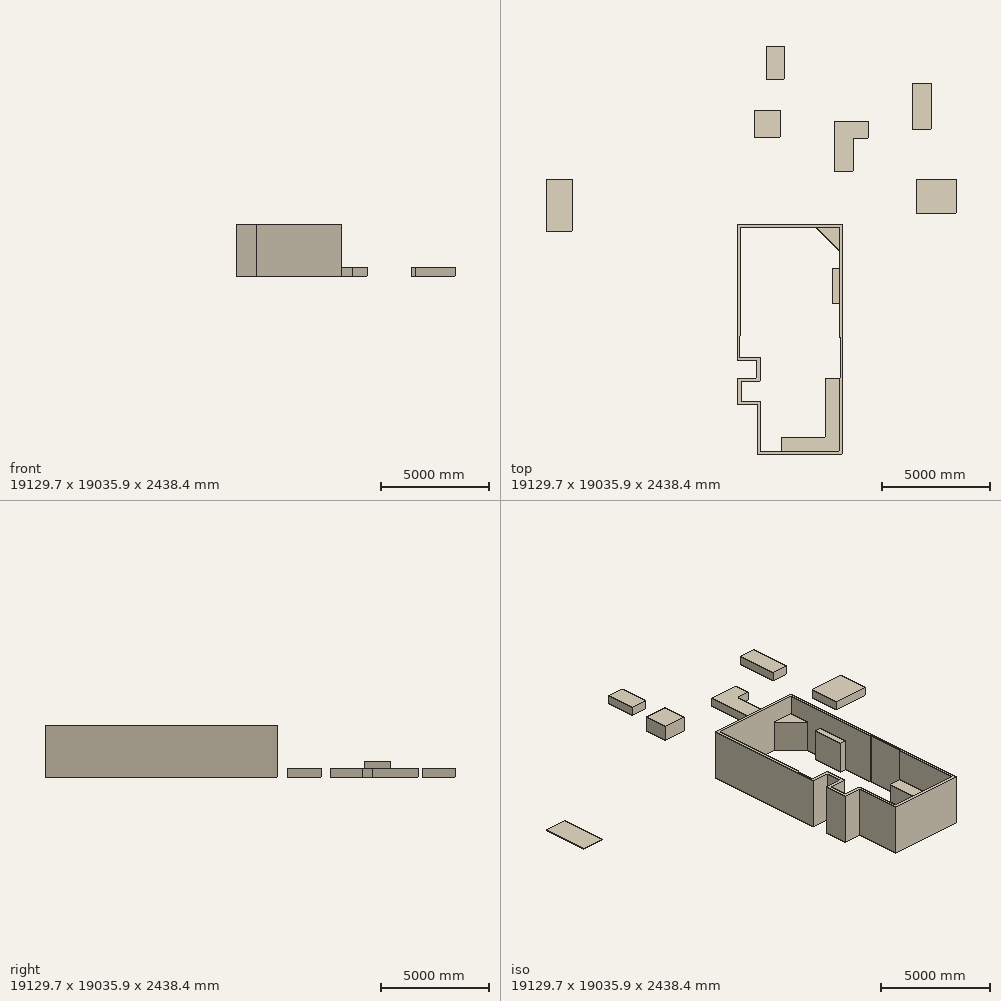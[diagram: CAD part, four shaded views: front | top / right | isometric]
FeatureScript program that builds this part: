
annotation { "Feature Type Name" : "Feature", "Feature Type Description" : "" }
export const myFeature = defineFeature(function(context is Context, id is Id, definition is map)
    precondition{}
    {
        {
            var Q0;
            Q0=qCreatedBy(makeId("Top.planeOp"),FACE);
            var sketch = newSketch(context, id + "F0", { "sketchPlane" : qUnion([Q0])});
            skLineSegment(sketch, "E0", {"start": v(-32.68, 52.66) * mm, "end": v(4583.77, 52.66) * mm});
            skLineSegment(sketch, "E1", {"start": v(4583.77, -10393.09) * mm, "end": v(4583.77, 52.66) * mm});
            skLineSegment(sketch, "E2", {"start": v(-32.68, 52.66) * mm, "end": v(-32.68, -5027.34) * mm});
            skLineSegment(sketch, "E3", {"start": v(-32.68, -5027.34) * mm, "end": v(-32.68, -6017.94) * mm});
            skLineSegment(sketch, "E4", {"start": v(-32.68, -6017.94) * mm, "end": v(894.42, -6017.94) * mm});
            skLineSegment(sketch, "E5", {"start": v(894.42, -6017.94) * mm, "end": v(894.42, -7134.23) * mm});
            skLineSegment(sketch, "E6", {"start": v(894.42, -7134.23) * mm, "end": v(0, -7134.23) * mm});
            skLineSegment(sketch, "E7", {"start": v(0, -7134.23) * mm, "end": v(0, -8060.89) * mm});
            skLineSegment(sketch, "E8", {"start": v(0, -8060.89) * mm, "end": v(929.64, -8060.89) * mm});
            skLineSegment(sketch, "E9", {"start": v(929.64, -8060.89) * mm, "end": v(929.64, -10405.79) * mm});
            skLineSegment(sketch, "E10", {"start": v(929.64, -10393.09) * mm, "end": v(1878.67, -10393.09) * mm});
            skLineSegment(sketch, "E11", {"start": v(1878.67, -10393.09) * mm, "end": v(4583.77, -10393.09) * mm});
            skLineSegment(sketch, "E12.0", {"start": v(1878.67, -10545.49) * mm, "end": v(4736.17, -10545.49) * mm});
            skLineSegment(sketch, "E12.1", {"start": v(-185.08, -6170.34) * mm, "end": v(742.02, -6170.34) * mm});
            skLineSegment(sketch, "E12.2", {"start": v(-185.08, -5040.04) * mm, "end": v(-185.08, -6170.34) * mm});
            skLineSegment(sketch, "E12.3", {"start": v(-185.08, 205.06) * mm, "end": v(-185.08, -5040.04) * mm});
            skLineSegment(sketch, "E12.4", {"start": v(-185.08, 205.06) * mm, "end": v(4736.17, 205.06) * mm});
            skLineSegment(sketch, "E12.5", {"start": v(742.02, -6170.34) * mm, "end": v(742.02, -6981.83) * mm});
            skLineSegment(sketch, "E12.6", {"start": v(4736.17, -10545.49) * mm, "end": v(4736.17, 205.06) * mm});
            skLineSegment(sketch, "E12.7", {"start": v(742.02, -6981.83) * mm, "end": v(-152.4, -6981.83) * mm});
            skLineSegment(sketch, "E12.8", {"start": v(-152.4, -6981.83) * mm, "end": v(-152.4, -8213.29) * mm});
            skLineSegment(sketch, "E12.9", {"start": v(-152.4, -8213.29) * mm, "end": v(777.24, -8213.29) * mm});
            skLineSegment(sketch, "E12.10", {"start": v(777.24, -8213.29) * mm, "end": v(777.24, -10545.49) * mm});
            skLineSegment(sketch, "E12.11", {"start": v(777.24, -10545.49) * mm, "end": v(1878.67, -10545.49) * mm});
            skLineSegment(sketch, "E13.bottom", {"start": v(2045.21, 8490.4) * mm, "end": v(1165.74, 8490.4) * mm});
            skLineSegment(sketch, "E13.top", {"start": v(2045.21, 6960.06) * mm, "end": v(1165.74, 6960.06) * mm});
            skLineSegment(sketch, "E13.left", {"start": v(2045.21, 8490.4) * mm, "end": v(2045.21, 6960.06) * mm});
            skLineSegment(sketch, "E13.right", {"start": v(1165.74, 8490.4) * mm, "end": v(1165.74, 6960.06) * mm});
            skLineSegment(sketch, "E14", {"start": v(4358.78, 4979.33) * mm, "end": v(4358.78, 2667.93) * mm});
            skLineSegment(sketch, "E15", {"start": v(4358.78, 2667.93) * mm, "end": v(5238.26, 2667.93) * mm});
            skLineSegment(sketch, "E16", {"start": v(5238.26, 2667.93) * mm, "end": v(5238.26, 4179.23) * mm});
            skLineSegment(sketch, "E17", {"start": v(5238.26, 4179.23) * mm, "end": v(5927.23, 4179.23) * mm});
            skLineSegment(sketch, "E18", {"start": v(5927.23, 4179.23) * mm, "end": v(5927.23, 4979.33) * mm});
            skLineSegment(sketch, "E19", {"start": v(5927.23, 4979.33) * mm, "end": v(4358.78, 4979.33) * mm});
            skLineSegment(sketch, "E20", {"start": v(4583.77, 52.66) * mm, "end": v(3491.57, 52.66) * mm});
            skLineSegment(sketch, "E21", {"start": v(3491.57, 52.66) * mm, "end": v(4583.77, -1039.54) * mm});
            skLineSegment(sketch, "E22", {"start": v(4583.77, -1039.54) * mm, "end": v(4583.77, 52.66) * mm});
            skLineSegment(sketch, "E23", {"start": v(4583.77, -1039.54) * mm, "end": v(4583.77, -1852.34) * mm});
            skLineSegment(sketch, "E24", {"start": v(4583.77, -1852.34) * mm, "end": v(4253.57, -1852.34) * mm});
            skLineSegment(sketch, "E25", {"start": v(4253.57, -1852.34) * mm, "end": v(4253.57, -3503.34) * mm});
            skLineSegment(sketch, "E26", {"start": v(4253.57, -3503.34) * mm, "end": v(4583.77, -3503.34) * mm});
            skLineSegment(sketch, "E27", {"start": v(4583.77, -3503.34) * mm, "end": v(4583.77, -5090.84) * mm});
            skLineSegment(sketch, "E28", {"start": v(4583.77, -5090.84) * mm, "end": v(4583.77, -7014.89) * mm});
            skLineSegment(sketch, "E29", {"start": v(4583.77, -7014.89) * mm, "end": v(4583.77, -10393.09) * mm});
            skLineSegment(sketch, "E30.bottom", {"start": v(4583.77, -10393.09) * mm, "end": v(3948.77, -10393.09) * mm});
            skLineSegment(sketch, "E30.top", {"start": v(4583.77, -7014.89) * mm, "end": v(3948.77, -7014.89) * mm});
            skLineSegment(sketch, "E30.left", {"start": v(4583.77, -10393.09) * mm, "end": v(4583.77, -7014.89) * mm});
            skLineSegment(sketch, "E30.right", {"start": v(3948.77, -10393.09) * mm, "end": v(3948.77, -7014.89) * mm});
            skLineSegment(sketch, "E31.bottom", {"start": v(4583.77, -10393.09) * mm, "end": v(1878.67, -10393.09) * mm});
            skLineSegment(sketch, "E31.top", {"start": v(4583.77, -9758.09) * mm, "end": v(1878.67, -9758.09) * mm});
            skLineSegment(sketch, "E31.left", {"start": v(4583.77, -10393.09) * mm, "end": v(4583.77, -9758.09) * mm});
            skLineSegment(sketch, "E31.right", {"start": v(1878.67, -10393.09) * mm, "end": v(1878.67, -9758.09) * mm});
            skLineSegment(sketch, "E32.bottom", {"start": v(1849.43, 5483) * mm, "end": v(630.23, 5483) * mm});
            skLineSegment(sketch, "E32.top", {"start": v(1849.43, 4263.8) * mm, "end": v(630.23, 4263.8) * mm});
            skLineSegment(sketch, "E32.left", {"start": v(1849.43, 5483) * mm, "end": v(1849.43, 4263.8) * mm});
            skLineSegment(sketch, "E32.right", {"start": v(630.23, 5483) * mm, "end": v(630.23, 4263.8) * mm});
            skLineSegment(sketch, "E33.bottom", {"start": v(-32.68, -5027.34) * mm, "end": v(-82.32, -5027.34) * mm});
            skLineSegment(sketch, "E33.top", {"start": v(-32.68, -6018.85) * mm, "end": v(-82.32, -6018.85) * mm});
            skLineSegment(sketch, "E33.left", {"start": v(-32.68, -5027.34) * mm, "end": v(-32.68, -6018.85) * mm});
            skLineSegment(sketch, "E33.right", {"start": v(-82.32, -5027.34) * mm, "end": v(-82.32, -6018.85) * mm});
            skLineSegment(sketch, "E34.bottom", {"start": v(4583.77, -5090.84) * mm, "end": v(4636.79, -5090.84) * mm});
            skLineSegment(sketch, "E34.top", {"start": v(4583.77, -7014.89) * mm, "end": v(4636.79, -7014.89) * mm});
            skLineSegment(sketch, "E34.right", {"start": v(4636.79, -5090.84) * mm, "end": v(4636.79, -7014.89) * mm});
            skLineSegment(sketch, "E35.bottom", {"start": v(7988.37, 6757.19) * mm, "end": v(8867.85, 6757.19) * mm});
            skLineSegment(sketch, "E35.top", {"start": v(7988.37, 4626.76) * mm, "end": v(8867.85, 4626.76) * mm});
            skLineSegment(sketch, "E35.left", {"start": v(7988.37, 6757.19) * mm, "end": v(7988.37, 4626.76) * mm});
            skLineSegment(sketch, "E35.right", {"start": v(8867.85, 6757.19) * mm, "end": v(8867.85, 4626.76) * mm});
            skLineSegment(sketch, "E36.bottom", {"start": v(8172.4, 2261.77) * mm, "end": v(10052, 2261.77) * mm});
            skLineSegment(sketch, "E36.top", {"start": v(8172.4, 693.32) * mm, "end": v(10052, 693.32) * mm});
            skLineSegment(sketch, "E36.left", {"start": v(8172.4, 2261.77) * mm, "end": v(8172.4, 693.32) * mm});
            skLineSegment(sketch, "E36.right", {"start": v(10052, 2261.77) * mm, "end": v(10052, 693.32) * mm});
            skLineSegment(sketch, "E37.bottom", {"start": v(-9077.66, 2286.6) * mm, "end": v(-7858.46, 2286.6) * mm});
            skLineSegment(sketch, "E37.top", {"start": v(-9077.66, -151.8) * mm, "end": v(-7858.46, -151.8) * mm});
            skLineSegment(sketch, "E37.left", {"start": v(-9077.66, 2286.6) * mm, "end": v(-9077.66, -151.8) * mm});
            skLineSegment(sketch, "E37.right", {"start": v(-7858.46, 2286.6) * mm, "end": v(-7858.46, -151.8) * mm});
            skLineSegment(sketch, "E38", {"start": v(-20234.12, -1033.01) * mm, "end": v(-15617.67, -1033.01) * mm});
            skLineSegment(sketch, "E39", {"start": v(-15617.67, -11478.76) * mm, "end": v(-15617.67, -1033.01) * mm});
            skLineSegment(sketch, "E40", {"start": v(-20234.12, -1033.01) * mm, "end": v(-20234.12, -6113.01) * mm});
            skLineSegment(sketch, "E41", {"start": v(-20234.12, -6113.01) * mm, "end": v(-20234.12, -7103.61) * mm});
            skLineSegment(sketch, "E42", {"start": v(-20234.12, -7103.61) * mm, "end": v(-19307.02, -7103.61) * mm});
            skLineSegment(sketch, "E43", {"start": v(-19307.02, -7103.61) * mm, "end": v(-19307.02, -8259.31) * mm});
            skLineSegment(sketch, "E44", {"start": v(-15617.67, -1033.01) * mm, "end": v(-16709.87, -1033.01) * mm});
            skLineSegment(sketch, "E45", {"start": v(-15617.67, -2125.21) * mm, "end": v(-15617.67, -1033.01) * mm});
            skLineSegment(sketch, "E46", {"start": v(-15617.67, -2125.21) * mm, "end": v(-15617.67, -2938.01) * mm});
            skLineSegment(sketch, "E47", {"start": v(-15617.67, -2938.01) * mm, "end": v(-16087.57, -2938.01) * mm});
            skLineSegment(sketch, "E48", {"start": v(-16087.57, -2938.01) * mm, "end": v(-16087.57, -4589.01) * mm});
            skLineSegment(sketch, "E49", {"start": v(-16087.57, -4589.01) * mm, "end": v(-15617.67, -4589.01) * mm});
            skLineSegment(sketch, "E50", {"start": v(-15617.67, -4589.01) * mm, "end": v(-15617.67, -6176.51) * mm});
            skLineSegment(sketch, "E51", {"start": v(-15617.67, -6176.51) * mm, "end": v(-15617.67, -8100.56) * mm});
            skLineSegment(sketch, "E52", {"start": v(-15617.67, -8100.56) * mm, "end": v(-15617.67, -11478.76) * mm});
            skLineSegment(sketch, "E53.left", {"start": v(-15617.67, -11478.76) * mm, "end": v(-15617.67, -8100.56) * mm});
            skLineSegment(sketch, "E54.left", {"start": v(-15617.67, -11478.76) * mm, "end": v(-15617.67, -10843.76) * mm});
            skLineSegment(sketch, "E55.bottom", {"start": v(-20234.12, -6113.01) * mm, "end": v(-20283.76, -6113.01) * mm});
            skLineSegment(sketch, "E55.top", {"start": v(-20234.12, -7104.52) * mm, "end": v(-20283.76, -7104.52) * mm});
            skLineSegment(sketch, "E55.left", {"start": v(-20234.12, -6113.01) * mm, "end": v(-20234.12, -7104.52) * mm});
            skLineSegment(sketch, "E55.right", {"start": v(-20283.76, -6113.01) * mm, "end": v(-20283.76, -7104.52) * mm});
            skLineSegment(sketch, "E56.bottom", {"start": v(-15617.67, -6176.51) * mm, "end": v(-15564.65, -6176.51) * mm});
            skLineSegment(sketch, "E56.top", {"start": v(-15617.67, -8100.56) * mm, "end": v(-15564.65, -8100.56) * mm});
            skLineSegment(sketch, "E56.right", {"start": v(-15564.65, -6176.51) * mm, "end": v(-15564.65, -8100.56) * mm});
            skLineSegment(sketch, "E57", {"start": v(-15617.67, -11656.56) * mm, "end": v(-15617.67, -14666.46) * mm});
            skLineSegment(sketch, "E58", {"start": v(-15617.67, -14666.46) * mm, "end": v(-26196.77, -14666.46) * mm});
            skLineSegment(sketch, "E59", {"start": v(-26196.77, -14666.46) * mm, "end": v(-26196.77, -11575.1) * mm});
            skLineSegment(sketch, "E60", {"start": v(-19976.94, -9295.95) * mm, "end": v(-19976.94, -11467.65) * mm});
            skLineSegment(sketch, "E61", {"start": v(-19976.94, -11467.65) * mm, "end": v(-19214.94, -11467.65) * mm});
            skLineSegment(sketch, "E62", {"start": v(-19214.94, -11467.65) * mm, "end": v(-19214.94, -11645.45) * mm});
            skLineSegment(sketch, "E63", {"start": v(-19214.94, -11645.45) * mm, "end": v(-19976.94, -11645.45) * mm});
            skLineSegment(sketch, "E64", {"start": v(-19976.94, -11645.45) * mm, "end": v(-19976.94, -12610.65) * mm});
            skLineSegment(sketch, "E65", {"start": v(-21170.74, -12610.65) * mm, "end": v(-21170.74, -11318.42) * mm});
            skLineSegment(sketch, "E66", {"start": v(-21170.74, -11318.42) * mm, "end": v(-22002.6, -11318.42) * mm});
            skLineSegment(sketch, "E67", {"start": v(-22002.6, -11318.42) * mm, "end": v(-22002.6, -10705.65) * mm});
            skLineSegment(sketch, "E68", {"start": v(-22002.6, -10705.65) * mm, "end": v(-23291.64, -10705.65) * mm});
            skLineSegment(sketch, "E69", {"start": v(-23291.64, -10705.65) * mm, "end": v(-23291.64, -10591.35) * mm});
            skLineSegment(sketch, "E70", {"start": v(-23291.64, -10591.35) * mm, "end": v(-22875.72, -10591.35) * mm});
            skLineSegment(sketch, "E71", {"start": v(-19307.02, -8259.31) * mm, "end": v(-19522.92, -8259.31) * mm});
            skLineSegment(sketch, "E72", {"start": v(-19522.92, -8259.31) * mm, "end": v(-19522.92, -7221.09) * mm});
            skLineSegment(sketch, "E73", {"start": v(-19522.92, -7221.09) * mm, "end": v(-23048.75, -7221.09) * mm});
            skLineSegment(sketch, "E74", {"start": v(-24507.67, -10608.81) * mm, "end": v(-24507.67, -10761.21) * mm});
            skLineSegment(sketch, "E75", {"start": v(-24507.67, -10761.21) * mm, "end": v(-26196.77, -10761.21) * mm});
            skLineSegment(sketch, "E76", {"start": v(-26196.77, -10761.21) * mm, "end": v(-26196.77, -11575.1) * mm});
            skLineSegment(sketch, "E77.bottom", {"start": v(-23048.75, -7221.09) * mm, "end": v(-22489.95, -7221.09) * mm});
            skLineSegment(sketch, "E77.top", {"start": v(-23048.75, -8021.19) * mm, "end": v(-22489.95, -8021.19) * mm});
            skLineSegment(sketch, "E77.left", {"start": v(-23048.75, -7221.09) * mm, "end": v(-23048.75, -8021.19) * mm});
            skLineSegment(sketch, "E77.right", {"start": v(-22489.95, -7221.09) * mm, "end": v(-22489.95, -8021.19) * mm});
            skLineSegment(sketch, "E78", {"start": v(-21170.74, -12610.65) * mm, "end": v(-19976.94, -12610.65) * mm});
            skLineSegment(sketch, "E79.bottom", {"start": v(-21675.57, -8281.54) * mm, "end": v(-21351.72, -8281.54) * mm});
            skLineSegment(sketch, "E79.top", {"start": v(-21675.57, -8154.54) * mm, "end": v(-21351.72, -8154.54) * mm});
            skLineSegment(sketch, "E79.left", {"start": v(-21675.57, -8281.54) * mm, "end": v(-21675.57, -8154.54) * mm});
            skLineSegment(sketch, "E79.right", {"start": v(-21351.72, -8281.54) * mm, "end": v(-21351.72, -8154.54) * mm});
            skLineSegment(sketch, "E80", {"start": v(-20203.95, -9168.95) * mm, "end": v(-20962.78, -9168.95) * mm});
            skLineSegment(sketch, "E81", {"start": v(-20962.78, -9168.95) * mm, "end": v(-21216.78, -9168.95) * mm});
            skLineSegment(sketch, "E82", {"start": v(-21216.78, -9168.95) * mm, "end": v(-21908.93, -9168.95) * mm});
            skLineSegment(sketch, "E83", {"start": v(-21908.93, -9168.95) * mm, "end": v(-22875.72, -9168.95) * mm});
            skLineSegment(sketch, "E84", {"start": v(-22875.72, -9168.95) * mm, "end": v(-22875.72, -10591.35) * mm});
            skLineSegment(sketch, "E85", {"start": v(-23048.75, -8021.19) * mm, "end": v(-23048.75, -8135.49) * mm});
            skLineSegment(sketch, "E86", {"start": v(-23048.75, -8135.49) * mm, "end": v(-22891.6, -8135.49) * mm});
            skLineSegment(sketch, "E87", {"start": v(-22891.6, -8135.49) * mm, "end": v(-22891.6, -8281.54) * mm});
            skLineSegment(sketch, "E88", {"start": v(-22891.6, -8281.54) * mm, "end": v(-23158.3, -8281.54) * mm});
            skLineSegment(sketch, "E89", {"start": v(-23158.3, -8281.54) * mm, "end": v(-23158.3, -7246.49) * mm});
            skLineSegment(sketch, "E90", {"start": v(-23158.3, -7246.49) * mm, "end": v(-24660.07, -7246.49) * mm});
            skLineSegment(sketch, "E91", {"start": v(-24660.07, -7246.49) * mm, "end": v(-24660.07, -8446.64) * mm});
            skLineSegment(sketch, "E92", {"start": v(-24660.07, -8446.64) * mm, "end": v(-24660.07, -8868.67) * mm});
            skLineSegment(sketch, "E93", {"start": v(-24660.07, -8868.67) * mm, "end": v(-24660.07, -9973.81) * mm});
            skLineSegment(sketch, "E94", {"start": v(-20203.95, -9168.95) * mm, "end": v(-19307.02, -9168.95) * mm});
            skLineSegment(sketch, "E95", {"start": v(-19307.02, -9168.95) * mm, "end": v(-19307.02, -9295.95) * mm});
            skLineSegment(sketch, "E96", {"start": v(-19307.02, -9295.95) * mm, "end": v(-19976.94, -9295.95) * mm});
            skLineSegment(sketch, "E97", {"start": v(-15617.67, -11478.76) * mm, "end": v(-18329.12, -11478.76) * mm});
            skLineSegment(sketch, "E98", {"start": v(-18329.12, -11478.76) * mm, "end": v(-18329.12, -11656.56) * mm});
            skLineSegment(sketch, "E99", {"start": v(-18329.12, -11656.56) * mm, "end": v(-15617.67, -11656.56) * mm});
            skLineSegment(sketch, "E100", {"start": v(-24507.67, -10608.81) * mm, "end": v(-25269.67, -10608.81) * mm});
            skLineSegment(sketch, "E101", {"start": v(-25269.67, -10608.81) * mm, "end": v(-25269.67, -9973.81) * mm});
            skLineSegment(sketch, "E102", {"start": v(-25269.67, -9973.81) * mm, "end": v(-24660.07, -9973.81) * mm});
            skLineSegment(sketch, "E103", {"start": v(-21908.93, -9283.25) * mm, "end": v(-22721.73, -9283.25) * mm});
            skLineSegment(sketch, "E104", {"start": v(-22721.73, -9283.25) * mm, "end": v(-22721.73, -10523.09) * mm});
            skLineSegment(sketch, "E105", {"start": v(-22721.73, -10523.09) * mm, "end": v(-21859.72, -10523.09) * mm});
            skLineSegment(sketch, "E106", {"start": v(-21908.93, -9283.25) * mm, "end": v(-21908.93, -9168.95) * mm});
            skLineSegment(sketch, "E107", {"start": v(-21859.72, -10523.09) * mm, "end": v(-21859.72, -11189.84) * mm});
            skLineSegment(sketch, "E108", {"start": v(-21859.72, -11189.84) * mm, "end": v(-21124.7, -11189.84) * mm});
            skLineSegment(sketch, "E109", {"start": v(-21124.7, -11189.84) * mm, "end": v(-21124.7, -9283.25) * mm});
            skLineSegment(sketch, "E110", {"start": v(-21124.7, -9283.25) * mm, "end": v(-21216.78, -9283.25) * mm});
            skLineSegment(sketch, "E111", {"start": v(-21216.78, -9283.25) * mm, "end": v(-21216.78, -9168.95) * mm});
            skLineSegment(sketch, "E112.bottom", {"start": v(2167.6, -7507.01) * mm, "end": v(2958.17, -7507.01) * mm});
            skLineSegment(sketch, "E112.top", {"start": v(2167.6, -8767.49) * mm, "end": v(2958.17, -8767.49) * mm});
            skLineSegment(sketch, "E112.left", {"start": v(2167.6, -7507.01) * mm, "end": v(2167.6, -8767.49) * mm});
            skLineSegment(sketch, "E112.right", {"start": v(2958.17, -7507.01) * mm, "end": v(2958.17, -8767.49) * mm});
            skSolve(sketch);
        }
        {
            var Q0;
            Q0=makeQuery(id+"F0.imprint","IMPRINT",FACE,{"disambiguationData":[TD([[makeQuery(id+"F0.imprint","IMPRINT",EDGE,{"derivedFrom":sQuery(id+"F0.wireOp",EDGE,"E14")}),1.0]])]});
            extrude(context, id + "F1", {"entities" : qUnion([Q0]), "depth" : 428.62 * mm, "offsetDistance" : 25.4 * mm});
        }
        {
            var Q0;
            Q0=makeQuery(id+"F0.imprint","IMPRINT",FACE,{"disambiguationData":[TD([[makeQuery(id+"F0.imprint","IMPRINT",EDGE,{"derivedFrom":sQuery(id+"F0.wireOp",EDGE,"E32.bottom")}),1.0]])]});
            extrude(context, id + "F2", {"entities" : qUnion([Q0]), "depth" : 736.6 * mm, "offsetDistance" : 25.4 * mm});
        }
        {
            var Q0;
            Q0=makeQuery(id+"F0.imprint","IMPRINT",FACE,{"disambiguationData":[TD([[makeQuery(id+"F0.imprint","IMPRINT",EDGE,{"derivedFrom":sQuery(id+"F0.wireOp",EDGE,"E13.bottom")}),1.0]])]});
            extrude(context, id + "F3", {"entities" : qUnion([Q0]), "depth" : 428.62 * mm, "offsetDistance" : 25.4 * mm});
        }
        {
            var Q0;
            {var subQ16=sQuery(id+"F0.wireOp",EDGE,"E2");Q0=makeQuery(id+"F0.imprint","IMPRINT",FACE,{"disambiguationData":[TD([[makeQuery(id+"F0.imprint","IMPRINT",EDGE,{"derivedFrom":subQ16}),-1.0]])]});}
            extrude(context, id + "F4", {"entities" : qUnion([Q0]), "depth" : 2438.4 * mm, "offsetDistance" : 25.4 * mm});
        }
        {
            var Q0;
            {var subQ3=sQuery(id+"F0.wireOp",EDGE,"E21");Q0=makeQuery(id+"F0.imprint","IMPRINT",FACE,{"disambiguationData":[TD([[makeQuery(id+"F0.imprint","IMPRINT",EDGE,{"derivedFrom":subQ3}),1.0]])]});}
            extrude(context, id + "F5", {"entities" : qUnion([Q0]), "operationType" : NewBodyOperationType.ADD, "depth" : 1524 * mm, "offsetDistance" : 25.4 * mm});
        }
        {
            var Q0;
            {var subQ3=sQuery(id+"F0.wireOp",EDGE,"E30.top");Q0=makeQuery(id+"F0.imprint","IMPRINT",FACE,{"disambiguationData":[TD([[makeQuery(id+"F0.imprint","IMPRINT",EDGE,{"derivedFrom":subQ3}),1.0]])]});}
            var Q1;
            {var subQ0=sQuery(id+"F0.wireOp",EDGE,"E31.top");var subQ1=sQuery(id+"F0.wireOp",EDGE,"E1");var subQ2=makeQuery(id+"F0.imprint","INTERSECT",VERTEX,{"derivedFrom":[subQ1,subQ0]});Q1=makeQuery(id+"F0.imprint","IMPRINT",FACE,{"disambiguationData":[TD([[makeQuery(id+"F0.imprint","IMPRINT",EDGE,{"disambiguationData":[TD([[subQ2,1.0]])],"derivedFrom":subQ1}),1.0]])]});}
            var Q2;
            {var subQ0=sQuery(id+"F0.wireOp",EDGE,"E31.right");Q2=makeQuery(id+"F0.imprint","IMPRINT",FACE,{"disambiguationData":[TD([[makeQuery(id+"F0.imprint","IMPRINT",EDGE,{"derivedFrom":subQ0}),-1.0]])]});}
            extrude(context, id + "F6", {"entities" : qUnion([Q0, Q1, Q2]), "operationType" : NewBodyOperationType.ADD, "depth" : 901.7 * mm, "offsetDistance" : 25.4 * mm});
        }
        {
            var Q0;
            {var subQ0=sQuery(id+"F0.wireOp",EDGE,"E24");Q0=makeQuery(id+"F0.imprint","IMPRINT",FACE,{"disambiguationData":[TD([[makeQuery(id+"F0.imprint","IMPRINT",EDGE,{"derivedFrom":subQ0}),1.0]])]});}
            extrude(context, id + "F7", {"entities" : qUnion([Q0]), "operationType" : NewBodyOperationType.ADD, "depth" : 1524 * mm, "offsetDistance" : 25.4 * mm});
        }
        {
            var Q0;
            Q0=makeQuery(id+"F0.imprint","IMPRINT",FACE,{"disambiguationData":[TD([[makeQuery(id+"F0.imprint","IMPRINT",EDGE,{"derivedFrom":sQuery(id+"F0.wireOp",EDGE,"E35.bottom")}),-1.0]])]});
            extrude(context, id + "F8", {"entities" : qUnion([Q0]), "depth" : 428.62 * mm, "offsetDistance" : 25.4 * mm});
        }
        {
            var Q0;
            Q0=makeQuery(id+"F0.imprint","IMPRINT",FACE,{"disambiguationData":[TD([[makeQuery(id+"F0.imprint","IMPRINT",EDGE,{"derivedFrom":sQuery(id+"F0.wireOp",EDGE,"E36.bottom")}),-1.0]])]});
            extrude(context, id + "F9", {"entities" : qUnion([Q0]), "depth" : 428.62 * mm, "offsetDistance" : 25.4 * mm});
        }
        {
            var Q0;
            Q0=makeQuery(id+"F0.imprint","IMPRINT",FACE,{"disambiguationData":[TD([[makeQuery(id+"F0.imprint","IMPRINT",EDGE,{"derivedFrom":sQuery(id+"F0.wireOp",EDGE,"E37.bottom")}),-1.0]])]});
            extrude(context, id + "F10", {"entities" : qUnion([Q0]), "depth" : 6.35 * mm, "offsetDistance" : 25.4 * mm});
        }
    });
